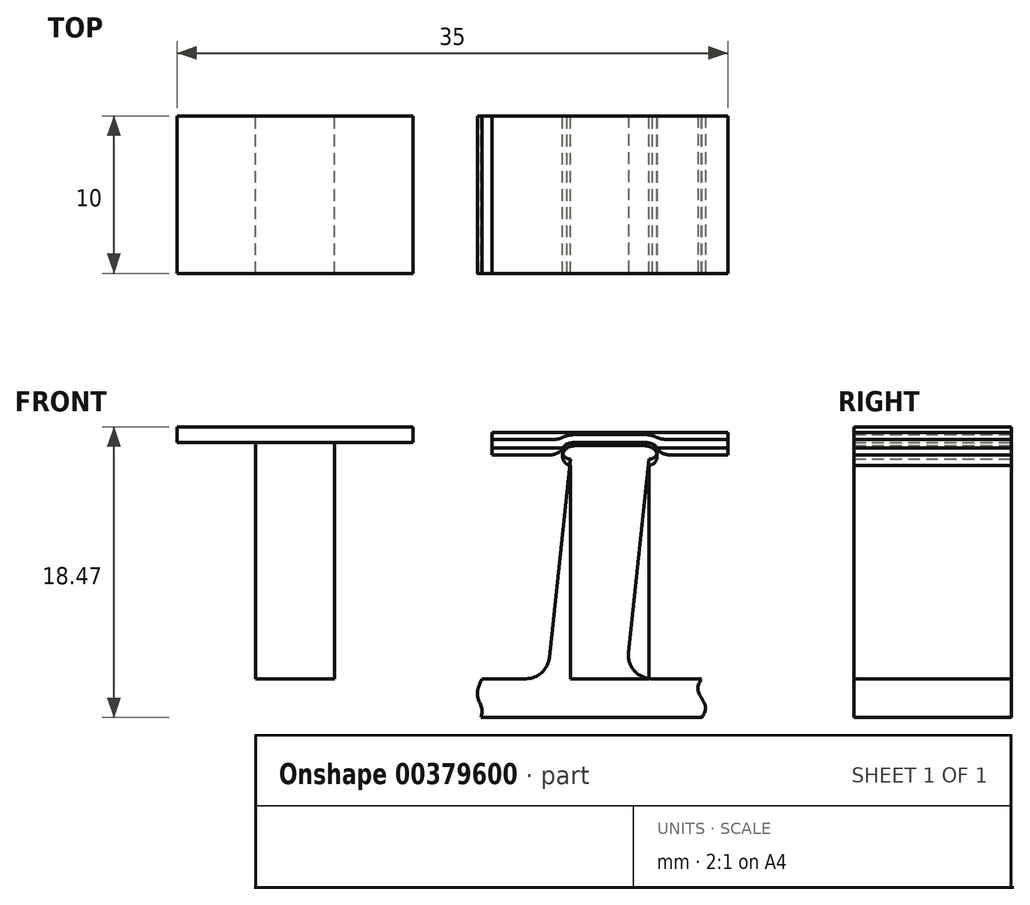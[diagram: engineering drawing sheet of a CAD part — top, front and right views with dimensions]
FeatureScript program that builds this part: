
annotation { "Feature Type Name" : "Feature", "Feature Type Description" : "" }
export const myFeature = defineFeature(function(context is Context, id is Id, definition is map)
    precondition{}
    {
        {
            var Q0;
            Q0=qCreatedBy(makeId("Front.planeOp"),FACE);
            var sketch = newSketch(context, id + "F0", { "sketchPlane" : qUnion([Q0])});
            skLineSegment(sketch, "E0", {"start": v(-65, 0) * mm, "end": v(-65, -5) * mm});
            skLineSegment(sketch, "E1", {"start": v(-65, -5) * mm, "end": v(-50, -5) * mm});
            skLineSegment(sketch, "E2", {"start": v(-50, -5) * mm, "end": v(-50, 0) * mm});
            skArc(sketch, "E3", {"start": v(-65, 0) * mm, "mid": v(-57.5, -1.46) * mm, "end": v(-50, 0) * mm});
            skLineSegment(sketch, "E4.bottom", {"start": v(-65, 4) * mm, "end": v(-50, 4) * mm, "construction": true});
            skLineSegment(sketch, "E4.top", {"start": v(-65, 3) * mm, "end": v(-50, 3) * mm, "construction": true});
            skLineSegment(sketch, "E4.left", {"start": v(-65, 4) * mm, "end": v(-65, 3) * mm});
            skLineSegment(sketch, "E4.right", {"start": v(-50, 4) * mm, "end": v(-50, 3) * mm});
            skLineSegment(sketch, "E5.bottom", {"start": v(-65, 4.25) * mm, "end": v(-50, 4.25) * mm, "construction": true});
            skLineSegment(sketch, "E5.top", {"start": v(-65, 4.05) * mm, "end": v(-50, 4.05) * mm, "construction": true});
            skLineSegment(sketch, "E5.left", {"start": v(-65, 4.25) * mm, "end": v(-65, 4.05) * mm});
            skLineSegment(sketch, "E5.right", {"start": v(-50, 4.25) * mm, "end": v(-50, 4.05) * mm});
            skLineSegment(sketch, "E6", {"start": v(-65, 7.25) * mm, "end": v(-65, 9.75) * mm});
            skLineSegment(sketch, "E7", {"start": v(-65, 9.75) * mm, "end": v(-50, 9.75) * mm});
            skLineSegment(sketch, "E8", {"start": v(-50, 9.75) * mm, "end": v(-50, 7.25) * mm});
            skArc(sketch, "E9", {"start": v(-65, 7.25) * mm, "mid": v(-57.5, 5.8) * mm, "end": v(-50, 7.25) * mm});
            skArc(sketch, "E10", {"start": v(-65, 3) * mm, "mid": v(-57.5, 1.54) * mm, "end": v(-50, 3) * mm});
            skArc(sketch, "E11", {"start": v(-65, 4) * mm, "mid": v(-57.5, 2.54) * mm, "end": v(-50, 4) * mm});
            skArc(sketch, "E12", {"start": v(-65, 4.05) * mm, "mid": v(-57.5, 2.6) * mm, "end": v(-50, 4.05) * mm});
            skArc(sketch, "E13", {"start": v(-65, 4.25) * mm, "mid": v(-57.5, 2.8) * mm, "end": v(-50, 4.25) * mm});
            skSolve(sketch);
        }
        {
            var Q0;
            Q0=qCreatedBy(makeId("Top.planeOp"),FACE);
            var sketch = newSketch(context, id + "F1", { "sketchPlane" : qUnion([Q0])});
            skLineSegment(sketch, "E14", {"start": v(-40, 10) * mm, "end": v(-40, -10) * mm});
            skLineSegment(sketch, "E15", {"start": v(-40, -10) * mm, "end": v(-30, -10) * mm});
            skLineSegment(sketch, "E16", {"start": v(-30, -10) * mm, "end": v(-15, -5) * mm});
            skLineSegment(sketch, "E17", {"start": v(-15, -5) * mm, "end": v(-15, 5) * mm});
            skLineSegment(sketch, "E18", {"start": v(-15, 5) * mm, "end": v(-30, 10) * mm});
            skLineSegment(sketch, "E19", {"start": v(-30, 10) * mm, "end": v(-40, 10) * mm});
            skPoint(sketch, "E20", {"position": v(-40, 0) * mm});
            skPoint(sketch, "E21", {"position": v(-15, 0) * mm});
            skCircle(sketch, "E22", {"center": v(0, 0) * mm, "radius": 15 * mm, "construction": true});
            skLineSegment(sketch, "E23.1.0", {"start": v(-35.36, -21.21) * mm, "end": v(-21.21, -35.36) * mm});
            skLineSegment(sketch, "E23.1.1", {"start": v(-14.14, -7.07) * mm, "end": v(-28.28, -14.14) * mm});
            skLineSegment(sketch, "E23.1.2", {"start": v(-28.28, -14.14) * mm, "end": v(-35.36, -21.21) * mm});
            skLineSegment(sketch, "E23.1.3", {"start": v(-7.07, -14.14) * mm, "end": v(-14.14, -7.07) * mm});
            skLineSegment(sketch, "E23.1.4", {"start": v(-14.14, -28.28) * mm, "end": v(-7.07, -14.14) * mm});
            skLineSegment(sketch, "E23.1.5", {"start": v(-21.21, -35.36) * mm, "end": v(-14.14, -28.28) * mm});
            skLineSegment(sketch, "E23.2.0", {"start": v(-10, -40) * mm, "end": v(10, -40) * mm});
            skLineSegment(sketch, "E23.2.1", {"start": v(-5, -15) * mm, "end": v(-10, -30) * mm});
            skLineSegment(sketch, "E23.2.2", {"start": v(-10, -30) * mm, "end": v(-10, -40) * mm});
            skLineSegment(sketch, "E23.2.3", {"start": v(5, -15) * mm, "end": v(-5, -15) * mm});
            skLineSegment(sketch, "E23.2.4", {"start": v(10, -30) * mm, "end": v(5, -15) * mm});
            skLineSegment(sketch, "E23.2.5", {"start": v(10, -40) * mm, "end": v(10, -30) * mm});
            skLineSegment(sketch, "E23.3.0", {"start": v(21.21, -35.36) * mm, "end": v(35.36, -21.21) * mm});
            skLineSegment(sketch, "E23.3.1", {"start": v(7.07, -14.14) * mm, "end": v(14.14, -28.28) * mm});
            skLineSegment(sketch, "E23.3.2", {"start": v(14.14, -28.28) * mm, "end": v(21.21, -35.36) * mm});
            skLineSegment(sketch, "E23.3.3", {"start": v(14.14, -7.07) * mm, "end": v(7.07, -14.14) * mm});
            skLineSegment(sketch, "E23.3.4", {"start": v(28.28, -14.14) * mm, "end": v(14.14, -7.07) * mm});
            skLineSegment(sketch, "E23.3.5", {"start": v(35.36, -21.21) * mm, "end": v(28.28, -14.14) * mm});
            skLineSegment(sketch, "E23.4.0", {"start": v(40, -10) * mm, "end": v(40, 10) * mm});
            skLineSegment(sketch, "E23.4.1", {"start": v(15, -5) * mm, "end": v(30, -10) * mm});
            skLineSegment(sketch, "E23.4.2", {"start": v(30, -10) * mm, "end": v(40, -10) * mm});
            skLineSegment(sketch, "E23.4.3", {"start": v(15, 5) * mm, "end": v(15, -5) * mm});
            skLineSegment(sketch, "E23.4.4", {"start": v(30, 10) * mm, "end": v(15, 5) * mm});
            skLineSegment(sketch, "E23.4.5", {"start": v(40, 10) * mm, "end": v(30, 10) * mm});
            skLineSegment(sketch, "E23.5.0", {"start": v(35.36, 21.21) * mm, "end": v(21.21, 35.36) * mm});
            skLineSegment(sketch, "E23.5.1", {"start": v(14.14, 7.07) * mm, "end": v(28.28, 14.14) * mm});
            skLineSegment(sketch, "E23.5.2", {"start": v(28.28, 14.14) * mm, "end": v(35.36, 21.21) * mm});
            skLineSegment(sketch, "E23.5.3", {"start": v(7.07, 14.14) * mm, "end": v(14.14, 7.07) * mm});
            skLineSegment(sketch, "E23.5.4", {"start": v(14.14, 28.28) * mm, "end": v(7.07, 14.14) * mm});
            skLineSegment(sketch, "E23.5.5", {"start": v(21.21, 35.36) * mm, "end": v(14.14, 28.28) * mm});
            skLineSegment(sketch, "E23.6.0", {"start": v(10, 40) * mm, "end": v(-10, 40) * mm});
            skLineSegment(sketch, "E23.6.1", {"start": v(5, 15) * mm, "end": v(10, 30) * mm});
            skLineSegment(sketch, "E23.6.2", {"start": v(10, 30) * mm, "end": v(10, 40) * mm});
            skLineSegment(sketch, "E23.6.3", {"start": v(-5, 15) * mm, "end": v(5, 15) * mm});
            skLineSegment(sketch, "E23.6.4", {"start": v(-10, 30) * mm, "end": v(-5, 15) * mm});
            skLineSegment(sketch, "E23.6.5", {"start": v(-10, 40) * mm, "end": v(-10, 30) * mm});
            skLineSegment(sketch, "E23.7.0", {"start": v(-21.21, 35.36) * mm, "end": v(-35.36, 21.21) * mm});
            skLineSegment(sketch, "E23.7.1", {"start": v(-7.07, 14.14) * mm, "end": v(-14.14, 28.28) * mm});
            skLineSegment(sketch, "E23.7.2", {"start": v(-14.14, 28.28) * mm, "end": v(-21.21, 35.36) * mm});
            skLineSegment(sketch, "E23.7.3", {"start": v(-14.14, 7.07) * mm, "end": v(-7.07, 14.14) * mm});
            skLineSegment(sketch, "E23.7.4", {"start": v(-28.28, 14.14) * mm, "end": v(-14.14, 7.07) * mm});
            skLineSegment(sketch, "E23.7.5", {"start": v(-35.36, 21.21) * mm, "end": v(-28.28, 14.14) * mm});
            skCircle(sketch, "E24", {"center": v(0, 0) * mm, "radius": 31.62 * mm, "construction": true});
            skLineSegment(sketch, "E25", {"start": v(0, 0) * mm, "end": v(-31.62, 0) * mm, "construction": true});
            skSolve(sketch);
        }
        {
            var Q0;
            Q0=qCreatedBy(makeId("Front.planeOp"),FACE);
            var sketch = newSketch(context, id + "F2", { "sketchPlane" : qUnion([Q0])});
            skArc(sketch, "E26", {"start": v(-31.62, 0) * mm, "mid": v(-23.31, -1.8) * mm, "end": v(-15, 0) * mm});
            skLineSegment(sketch, "E27", {"start": v(-31.62, 0) * mm, "end": v(-15, 0) * mm});
            skLineSegment(sketch, "E28", {"start": v(0, 0) * mm, "end": v(0, -10) * mm, "construction": true});
            skSolve(sketch);
        }
        {
            var Q0;
            Q0=qCreatedBy(makeId("Front.planeOp"),FACE);
            var sketch = newSketch(context, id + "F3", { "sketchPlane" : qUnion([Q0])});
            skLineSegment(sketch, "E29", {"start": v(-31.62, 0) * mm, "end": v(-40, 0) * mm});
            skLineSegment(sketch, "E30", {"start": v(-40, 0) * mm, "end": v(-40, -10) * mm});
            skLineSegment(sketch, "E31", {"start": v(-40, -10) * mm, "end": v(-15, -10) * mm});
            skLineSegment(sketch, "E32", {"start": v(-15, -10) * mm, "end": v(-15, 0) * mm});
            skArc(sketch, "E33", {"start": v(-31.62, 0) * mm, "mid": v(-23.31, -1.8) * mm, "end": v(-15, 0) * mm});
            skSolve(sketch);
        }
        {
            var Q0;
            Q0=qCreatedBy(makeId("Top.planeOp"),FACE);
            var sketch = newSketch(context, id + "F4", { "sketchPlane" : qUnion([Q0])});
            skLineSegment(sketch, "E34", {"start": v(-15, 5) * mm, "end": v(-31.62, 10) * mm});
            skLineSegment(sketch, "E35", {"start": v(-31.62, 10) * mm, "end": v(-31.62, 15) * mm});
            skLineSegment(sketch, "E36", {"start": v(-31.62, 15) * mm, "end": v(-11.62, 15) * mm});
            skLineSegment(sketch, "E37", {"start": v(-11.62, 15) * mm, "end": v(-11.62, -15) * mm});
            skLineSegment(sketch, "E38", {"start": v(-11.62, -15) * mm, "end": v(-31.62, -15) * mm});
            skLineSegment(sketch, "E39", {"start": v(-31.62, -15) * mm, "end": v(-31.62, -10) * mm});
            skLineSegment(sketch, "E40", {"start": v(-31.62, -10) * mm, "end": v(-15, -5) * mm});
            skLineSegment(sketch, "E41", {"start": v(-15, -5) * mm, "end": v(-15, 5) * mm});
            skSolve(sketch);
        }
        {
            var Q0;
            Q0=qCreatedBy(makeId("Front.planeOp"),FACE);
            var sketch = newSketch(context, id + "F5", { "sketchPlane" : qUnion([Q0])});
            skLineSegment(sketch, "E42", {"start": v(-65, 0) * mm, "end": v(-65, -15) * mm});
            skLineSegment(sketch, "E43", {"start": v(-65, -15) * mm, "end": v(-60, -15) * mm});
            skLineSegment(sketch, "E44", {"start": v(-60, -15) * mm, "end": v(-60, 0) * mm});
            skLineSegment(sketch, "E45", {"start": v(-60, 0) * mm, "end": v(-65, 0) * mm});
            skLineSegment(sketch, "E46", {"start": v(-45, -1.45) * mm, "end": v(-45, -15) * mm});
            skLineSegment(sketch, "E47", {"start": v(-45, -15) * mm, "end": v(-40, -15) * mm});
            skLineSegment(sketch, "E48", {"start": v(-40, -15) * mm, "end": v(-40, -1.45) * mm});
            skLineSegment(sketch, "E49", {"start": v(-44.7, -0.2) * mm, "end": v(-40.3, -0.2) * mm});
            skArc(sketch, "E50", {"start": v(-44.7, -0.2) * mm, "mid": v(-44.97, -0.24) * mm, "end": v(-45.22, -0.34) * mm});
            skArc(sketch, "E51", {"start": v(-39.78, -0.34) * mm, "mid": v(-40.03, -0.24) * mm, "end": v(-40.3, -0.2) * mm});
            skArc(sketch, "E52", {"start": v(-45.22, -0.34) * mm, "mid": v(-45.5, -0.97) * mm, "end": v(-45, -1.45) * mm});
            skArc(sketch, "E53", {"start": v(-40, -1.45) * mm, "mid": v(-39.5, -0.97) * mm, "end": v(-39.78, -0.34) * mm});
            skSolve(sketch);
        }
        {
            var Q0;
            Q0 = qSketchRegion(id + "F5", true);
            extrude(context, id + "F6", {"entities" : qUnion([Q0]), "endBound" : BoundingType.SYMMETRIC, "depth" : 10 * mm});
        }
        {
            var Q0;
            Q0=qCreatedBy(makeId("Front.planeOp"),FACE);
            var sketch = newSketch(context, id + "F7", { "sketchPlane" : qUnion([Q0])});
            skLineSegment(sketch, "E54.bottom", {"start": v(-70, 1) * mm, "end": v(-55, 1) * mm});
            skLineSegment(sketch, "E54.top", {"start": v(-70, 0) * mm, "end": v(-55, 0) * mm});
            skLineSegment(sketch, "E54.left", {"start": v(-70, 1) * mm, "end": v(-70, 0) * mm});
            skLineSegment(sketch, "E54.right", {"start": v(-55, 1) * mm, "end": v(-55, 0) * mm});
            skPoint(sketch, "E55", {"position": v(-62.5, 0) * mm});
            skLineSegment(sketch, "E56", {"start": v(-50, 0.66) * mm, "end": v(-35, 0.66) * mm});
            skLineSegment(sketch, "E57", {"start": v(-35, 0.66) * mm, "end": v(-35, -0.34) * mm});
            skLineSegment(sketch, "E58", {"start": v(-35, -0.34) * mm, "end": v(-39.78, -0.34) * mm});
            skLineSegment(sketch, "E59", {"start": v(-50, 0.66) * mm, "end": v(-50, -0.34) * mm});
            skLineSegment(sketch, "E60", {"start": v(-50, -0.34) * mm, "end": v(-45.22, -0.34) * mm});
            skArc(sketch, "E61", {"start": v(-44.7, -0.2) * mm, "mid": v(-44.97, -0.24) * mm, "end": v(-45.22, -0.34) * mm});
            skArc(sketch, "E62", {"start": v(-39.78, -0.34) * mm, "mid": v(-40.03, -0.24) * mm, "end": v(-40.3, -0.2) * mm});
            skLineSegment(sketch, "E63", {"start": v(-44.7, -0.2) * mm, "end": v(-40.3, -0.2) * mm});
            skSolve(sketch);
        }
        {
            var Q0;
            Q0 = qSketchRegion(id + "F7", true);
            extrude(context, id + "F8", {"entities" : qUnion([Q0]), "endBound" : BoundingType.SYMMETRIC, "depth" : 10 * mm});
        }
        {
            var Q0;
            Q0=qCreatedBy(makeId("Front.planeOp"),FACE);
            var sketch = newSketch(context, id + "F9", { "sketchPlane" : qUnion([Q0])});
            skLineSegment(sketch, "E64", {"start": v(-45, -15) * mm, "end": v(-40, -15) * mm, "construction": true});
            skLineSegment(sketch, "E65", {"start": v(-44.75, 0) * mm, "end": v(-40.25, 0) * mm});
            skLineSegment(sketch, "E66", {"start": v(-45, -1.05) * mm, "end": v(-40, -1.05) * mm, "construction": true});
            skPoint(sketch, "E67", {"position": v(-42.5, -1.05) * mm});
            skPoint(sketch, "E68", {"position": v(-42.5, 0) * mm});
            skLineSegment(sketch, "E69", {"start": v(-42.5, 0) * mm, "end": v(-42.5, -1.05) * mm, "construction": true});
            skArc(sketch, "E70", {"start": v(-45.2, -0.08) * mm, "mid": v(-45.5, -0.65) * mm, "end": v(-45, -1.05) * mm});
            skArc(sketch, "E71", {"start": v(-44.75, 0) * mm, "mid": v(-44.98, -0.02) * mm, "end": v(-45.2, -0.08) * mm});
            skArc(sketch, "E72", {"start": v(-40, -1.05) * mm, "mid": v(-39.5, -0.65) * mm, "end": v(-39.8, -0.08) * mm});
            skArc(sketch, "E73", {"start": v(-39.8, -0.08) * mm, "mid": v(-40.02, -0.02) * mm, "end": v(-40.25, 0) * mm});
            skLineSegment(sketch, "E74", {"start": v(-45, -1.05) * mm, "end": v(-46.49, -15) * mm});
            skLineSegment(sketch, "E75", {"start": v(-40, -1.05) * mm, "end": v(-41.49, -15) * mm});
            skLineSegment(sketch, "E76", {"start": v(-46.49, -15) * mm, "end": v(-50.63, -15) * mm});
            skLineSegment(sketch, "E77", {"start": v(-41.49, -15) * mm, "end": v(-36.68, -15) * mm});
            skLineSegment(sketch, "E78", {"start": v(-50.69, -17.47) * mm, "end": v(-36.64, -17.47) * mm});
            skFitSpline(sketch, "E79", {"points": [v(-50.63, -15) * mm, v(-50.91, -16.12) * mm, v(-50.63, -16.86) * mm, v(-50.69, -17.47) * mm], "startDerivative": vector(-1.28, -3.02) * mm, "endDerivative": vector(-0.57, -2.14) * mm});
            skFitSpline(sketch, "E80", {"points": [v(-36.68, -15) * mm, v(-36.9, -15.73) * mm, v(-36.44, -16.72) * mm, v(-36.64, -17.47) * mm], "startDerivative": vector(-1.3, -2.26) * mm, "endDerivative": vector(-1.22, -2.3) * mm});
            skSolve(sketch);
        }
        {
            var Q0;
            Q0 = qSketchRegion(id + "F9", true);
            extrude(context, id + "F10", {"entities" : qUnion([Q0]), "endBound" : BoundingType.SYMMETRIC, "depth" : 10 * mm});
        }
        {
            var Q0;
            Q0=qCreatedBy(makeId("Front.planeOp"),FACE);
            var sketch = newSketch(context, id + "F11", { "sketchPlane" : qUnion([Q0])});
            skLineSegment(sketch, "E81", {"start": v(-45.46, -0.8) * mm, "end": v(-50, -0.8) * mm});
            skLineSegment(sketch, "E82", {"start": v(-50, -0.8) * mm, "end": v(-50, 0.2) * mm});
            skLineSegment(sketch, "E83", {"start": v(-50, 0.2) * mm, "end": v(-45.72, 0.2) * mm});
            skArc(sketch, "E84", {"start": v(-44.75, 0.5) * mm, "mid": v(-45.26, 0.43) * mm, "end": v(-45.72, 0.2) * mm});
            skLineSegment(sketch, "E85", {"start": v(-44.75, 0.5) * mm, "end": v(-40.25, 0.5) * mm});
            skArc(sketch, "E86", {"start": v(-39.28, 0.2) * mm, "mid": v(-39.74, 0.43) * mm, "end": v(-40.25, 0.5) * mm});
            skLineSegment(sketch, "E87", {"start": v(-39.28, 0.2) * mm, "end": v(-35, 0.2) * mm});
            skLineSegment(sketch, "E88", {"start": v(-35, 0.2) * mm, "end": v(-35, -0.8) * mm});
            skLineSegment(sketch, "E89", {"start": v(-35, -0.8) * mm, "end": v(-39.54, -0.8) * mm});
            skArc(sketch, "E90", {"start": v(-45.2, -0.08) * mm, "mid": v(-45.5, -0.38) * mm, "end": v(-45.46, -0.8) * mm});
            skArc(sketch, "E91", {"start": v(-44.75, 0) * mm, "mid": v(-44.98, -0.02) * mm, "end": v(-45.2, -0.08) * mm});
            skArc(sketch, "E92", {"start": v(-39.8, -0.08) * mm, "mid": v(-40.02, -0.02) * mm, "end": v(-40.25, 0) * mm});
            skArc(sketch, "E93", {"start": v(-39.54, -0.8) * mm, "mid": v(-39.5, -0.38) * mm, "end": v(-39.8, -0.08) * mm});
            skLineSegment(sketch, "E94", {"start": v(-44.75, 0) * mm, "end": v(-40.25, 0) * mm});
            skSolve(sketch);
        }
        {
            var Q0;
            Q0 = qSketchRegion(id + "F11", true);
            extrude(context, id + "F12", {"entities" : qUnion([Q0]), "endBound" : BoundingType.SYMMETRIC, "depth" : 10 * mm});
        }
        {
            var Q0;
            Q0=makeQuery(id+"F12.opExtrude","SWEPT_EDGE",EDGE,{"disambiguationData":[OSD([sQuery(id+"F11.wireOp",EDGE,"E81"),sQuery(id+"F11.wireOp",EDGE,"E90")])]});
            var Q1;
            Q1=makeQuery(id+"F12.opExtrude","SWEPT_EDGE",EDGE,{"disambiguationData":[OSD([sQuery(id+"F11.wireOp",EDGE,"E89"),sQuery(id+"F11.wireOp",EDGE,"E93")])]});
            var Q2;
            Q2=makeQuery(id+"F12.opExtrude","SWEPT_EDGE",EDGE,{"disambiguationData":[OSD([sQuery(id+"F11.wireOp",EDGE,"E83"),sQuery(id+"F11.wireOp",EDGE,"E84")])]});
            var Q3;
            Q3=makeQuery(id+"F12.opExtrude","SWEPT_EDGE",EDGE,{"disambiguationData":[OSD([sQuery(id+"F11.wireOp",EDGE,"E86"),sQuery(id+"F11.wireOp",EDGE,"E87")])]});
            fillet(context, id + "F13", {"entities" : qUnion([Q0, Q1, Q2, Q3]), "radius" : 1 * mm, "tangentPropagation" : true, "allowEdgeOverflow" : false});
        }
        {
            var Q0;
            Q0=makeQuery(id+"F10.opExtrude","SWEPT_EDGE",EDGE,{"disambiguationData":[OSD([sQuery(id+"F9.wireOp",EDGE,"E75"),sQuery(id+"F9.wireOp",EDGE,"E77")])]});
            var Q1;
            Q1=makeQuery(id+"F10.opExtrude","SWEPT_EDGE",EDGE,{"disambiguationData":[OSD([sQuery(id+"F9.wireOp",EDGE,"E74"),sQuery(id+"F9.wireOp",EDGE,"E76")])]});
            fillet(context, id + "F14", {"entities" : qUnion([Q0, Q1]), "radius" : 1.5 * mm, "tangentPropagation" : true, "allowEdgeOverflow" : false});
        }
    });
